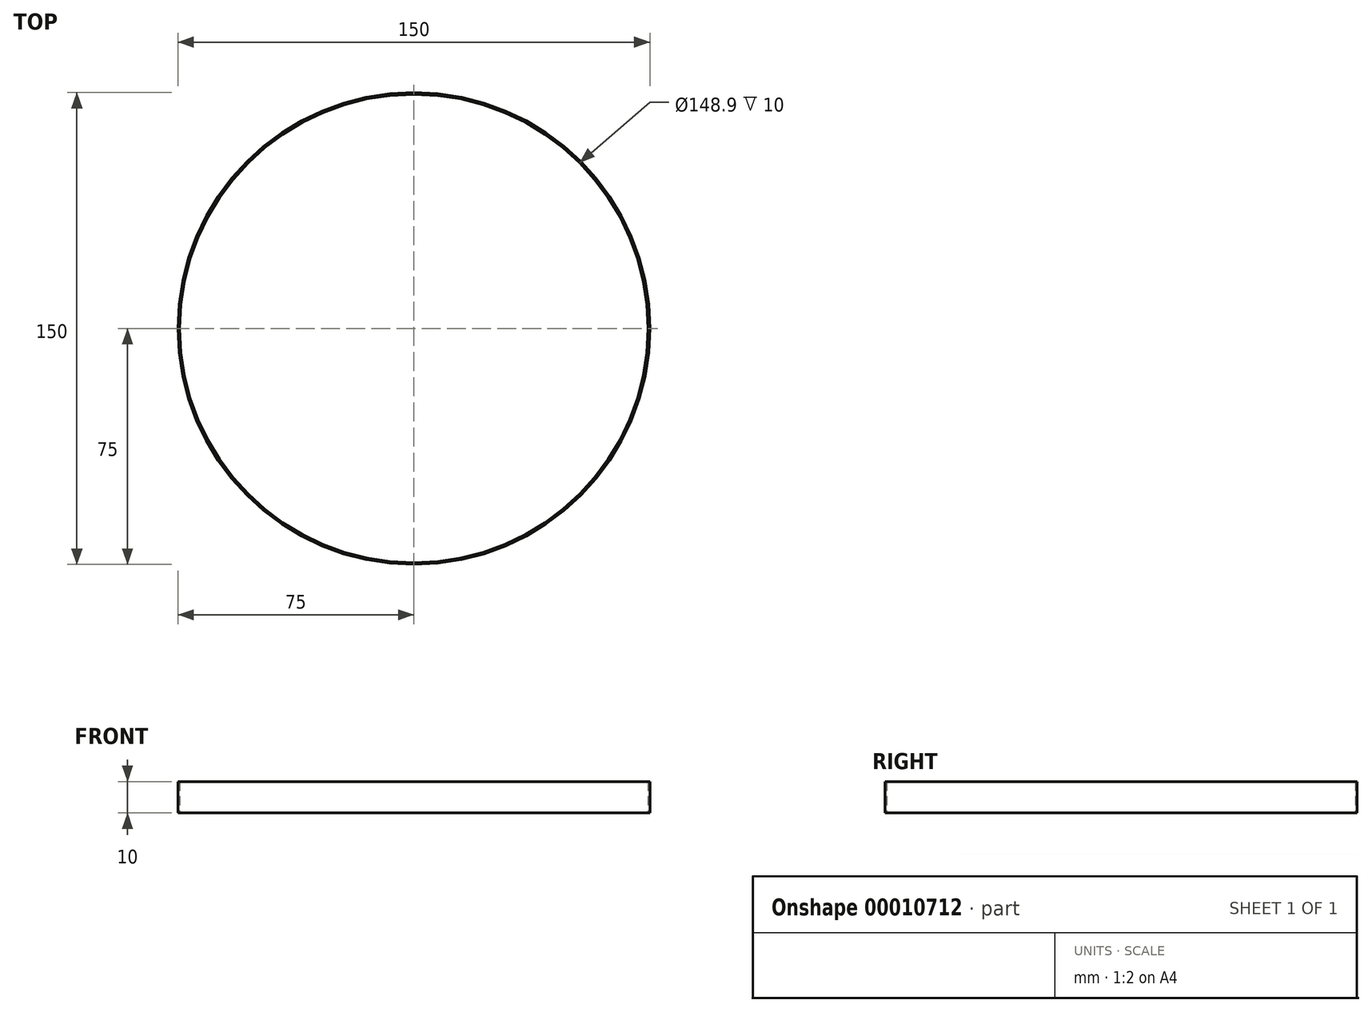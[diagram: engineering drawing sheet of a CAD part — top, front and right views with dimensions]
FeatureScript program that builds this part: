
annotation { "Feature Type Name" : "Feature", "Feature Type Description" : "" }
export const myFeature = defineFeature(function(context is Context, id is Id, definition is map)
    precondition{}
    {
        {
            var Q0;
            Q0=qCreatedBy(makeId("Top.planeOp"),FACE);
            var sketch = newSketch(context, id + "F0", { "sketchPlane" : qUnion([Q0])});
            skCircle(sketch, "E0", {"center": v(0, 0) * mm, "radius": 74.45 * mm});
            skCircle(sketch, "E1", {"center": v(0, 0) * mm, "radius": 75 * mm});
            skSolve(sketch);
        }
        {
            var Q0;
            Q0=makeQuery(id+"F0.imprint","IMPRINT",FACE,{"disambiguationData":[TD([[makeQuery(id+"F0.imprint","IMPRINT",EDGE,{"derivedFrom":sQuery(id+"F0.wireOp",EDGE,"E0")}),-1.0]])]});
            extrude(context, id + "F1", {"entities" : qUnion([Q0]), "depth" : 10 * mm});
        }
    });
